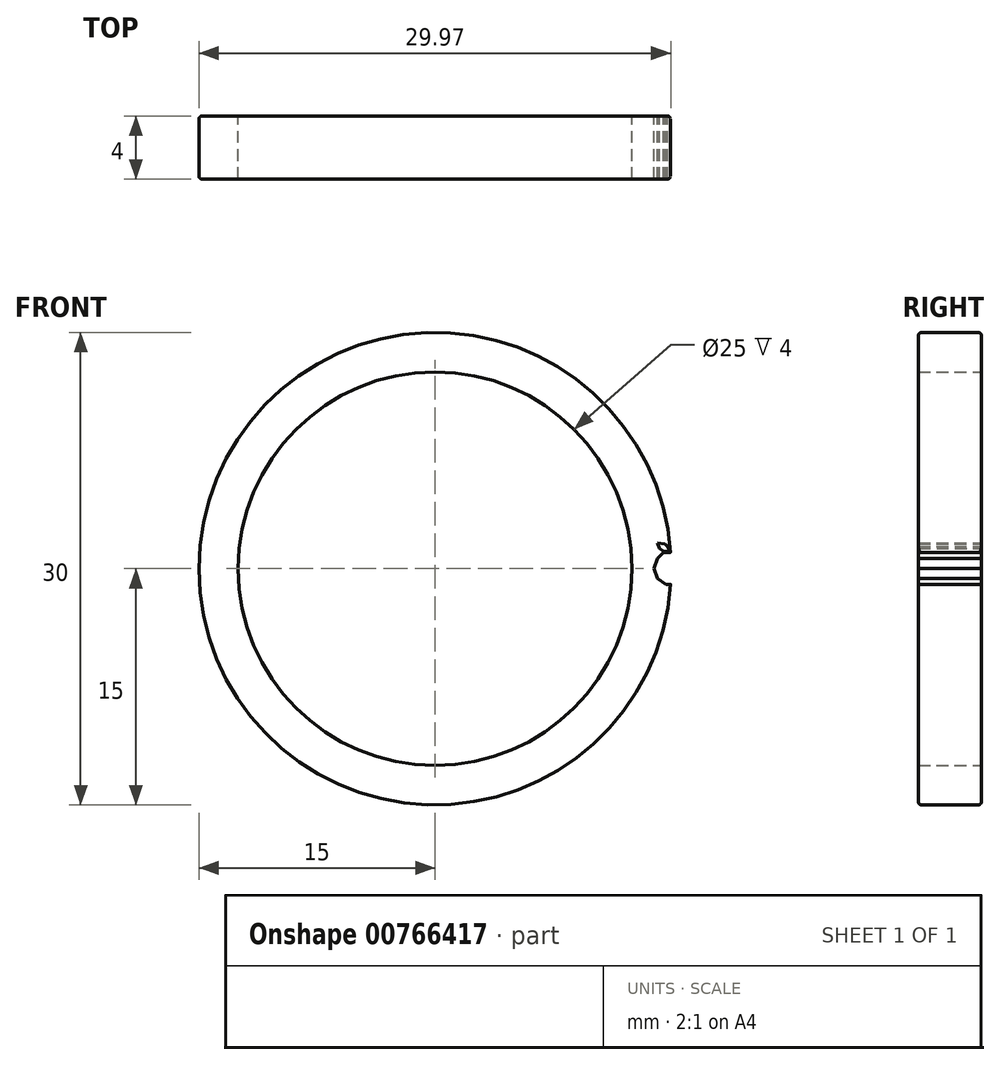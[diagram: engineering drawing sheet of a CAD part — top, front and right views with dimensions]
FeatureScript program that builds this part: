
annotation { "Feature Type Name" : "Feature", "Feature Type Description" : "" }
export const myFeature = defineFeature(function(context is Context, id is Id, definition is map)
    precondition{}
    {
        {
            var Q0;
            Q0=qCreatedBy(makeId("Front.planeOp"),FACE);
            var sketch = newSketch(context, id + "F0", { "sketchPlane" : qUnion([Q0])});
            skCircle(sketch, "E0", {"center": v(0, 0) * mm, "radius": 15 * mm});
            skCircle(sketch, "E1", {"center": v(0, 0) * mm, "radius": 12.5 * mm});
            skSolve(sketch);
        }
        {
            var Q0;
            Q0=qCreatedBy(makeId("Front.planeOp"),FACE);
            var sketch = newSketch(context, id + "F1", { "sketchPlane" : qUnion([Q0])});
            skLineSegment(sketch, "E2.0", {"start": v(14.65, -1) * mm, "end": v(14.12, -0.6) * mm});
            skLineSegment(sketch, "E2.1", {"start": v(14.12, -0.6) * mm, "end": v(13.9, 0.03) * mm});
            skLineSegment(sketch, "E2.2", {"start": v(13.9, 0.03) * mm, "end": v(14.12, 0.66) * mm});
            skLineSegment(sketch, "E2.3", {"start": v(14.12, 0.66) * mm, "end": v(14.5, 1.03) * mm});
            skLineSegment(sketch, "E2.5", {"start": v(15.42, 1.03) * mm, "end": v(15.86, 0.66) * mm});
            skLineSegment(sketch, "E2.6", {"start": v(15.86, 0.66) * mm, "end": v(16.07, 0.03) * mm});
            skLineSegment(sketch, "E2.7", {"start": v(16.07, 0.03) * mm, "end": v(15.86, -0.6) * mm});
            skLineSegment(sketch, "E2.8", {"start": v(15.86, -0.6) * mm, "end": v(15.32, -1) * mm});
            skLineSegment(sketch, "E2.9", {"start": v(15.32, -1) * mm, "end": v(14.65, -1) * mm});
            skLineSegment(sketch, "E3", {"start": v(14.5, 1.03) * mm, "end": v(14.99, 1.03) * mm});
            skLineSegment(sketch, "E4", {"start": v(14.99, 1.03) * mm, "end": v(15.42, 1.03) * mm});
            skLineSegment(sketch, "E5", {"start": v(14.93, 1.06) * mm, "end": v(14.77, 1.4) * mm});
            skLineSegment(sketch, "E6", {"start": v(14.77, 1.4) * mm, "end": v(14.6, 1.56) * mm});
            skLineSegment(sketch, "E7", {"start": v(14.6, 1.56) * mm, "end": v(14.13, 1.64) * mm});
            skLineSegment(sketch, "E8", {"start": v(14.13, 1.64) * mm, "end": v(14.25, 1.28) * mm});
            skLineSegment(sketch, "E9", {"start": v(14.25, 1.28) * mm, "end": v(14.53, 1.1) * mm});
            skLineSegment(sketch, "E10", {"start": v(14.53, 1.1) * mm, "end": v(14.93, 1.06) * mm});
            skLineSegment(sketch, "E11", {"start": v(15, 1.06) * mm, "end": v(15.36, 1.1) * mm});
            skLineSegment(sketch, "E12", {"start": v(15.36, 1.1) * mm, "end": v(15.57, 1.2) * mm});
            skLineSegment(sketch, "E13", {"start": v(15.57, 1.2) * mm, "end": v(15.81, 1.62) * mm});
            skLineSegment(sketch, "E14", {"start": v(15.81, 1.62) * mm, "end": v(15.43, 1.63) * mm});
            skLineSegment(sketch, "E15", {"start": v(15.43, 1.63) * mm, "end": v(15.17, 1.43) * mm});
            skLineSegment(sketch, "E16", {"start": v(15.17, 1.43) * mm, "end": v(15, 1.06) * mm});
            skSolve(sketch);
        }
        {
            var Q0;
            Q0 = qSketchRegion(id + "F0", true);
            extrude(context, id + "F2", {"entities" : qUnion([Q0]), "endBound" : BoundingType.SYMMETRIC, "depth" : 4 * mm, "offsetDistance" : 25 * mm});
        }
        {
            var Q0;
            Q0 = qSketchRegion(id + "F1", true);
            extrude(context, id + "F3", {"entities" : qUnion([Q0]), "endBound" : BoundingType.SYMMETRIC, "depth" : 4 * mm, "offsetDistance" : 25 * mm});
        }
        {
            var Q0;
            Q0=makeQuery(id+"F3.opExtrude","SWEPT_BODY",BODY,{"disambiguationData":[OSD([sQuery(id+"F1.wireOp",EDGE,"E2.0"),sQuery(id+"F1.wireOp",EDGE,"E2.1"),sQuery(id+"F1.wireOp",EDGE,"E2.2"),sQuery(id+"F1.wireOp",EDGE,"E2.3"),sQuery(id+"F1.wireOp",EDGE,"E2.5"),sQuery(id+"F1.wireOp",EDGE,"E2.6"),sQuery(id+"F1.wireOp",EDGE,"E2.7"),sQuery(id+"F1.wireOp",EDGE,"E2.8"),sQuery(id+"F1.wireOp",EDGE,"E2.9"),sQuery(id+"F1.wireOp",EDGE,"E3"),sQuery(id+"F1.wireOp",EDGE,"E4")])]});
            var Q1;
            Q1=makeQuery(id+"F3.opExtrude","SWEPT_BODY",BODY,{"disambiguationData":[OSD([sQuery(id+"F1.wireOp",EDGE,"E11"),sQuery(id+"F1.wireOp",EDGE,"E12"),sQuery(id+"F1.wireOp",EDGE,"E13"),sQuery(id+"F1.wireOp",EDGE,"E14"),sQuery(id+"F1.wireOp",EDGE,"E15"),sQuery(id+"F1.wireOp",EDGE,"E16")])]});
            var Q2;
            Q2=makeQuery(id+"F3.opExtrude","SWEPT_BODY",BODY,{"disambiguationData":[OSD([sQuery(id+"F1.wireOp",EDGE,"E5"),sQuery(id+"F1.wireOp",EDGE,"E6"),sQuery(id+"F1.wireOp",EDGE,"E7"),sQuery(id+"F1.wireOp",EDGE,"E8"),sQuery(id+"F1.wireOp",EDGE,"E9"),sQuery(id+"F1.wireOp",EDGE,"E10")])]});
            var Q3;
            Q3=makeQuery(id+"F2.opExtrude","SWEPT_BODY",BODY,{"disambiguationData":[OSD([sQuery(id+"F0.wireOp",EDGE,"E0"),sQuery(id+"F0.wireOp",EDGE,"E1")])]});
            booleanBodies(context, id + "F4", {"operationType" : BooleanOperationType.SUBTRACTION, "tools" : qUnion([Q0, Q1, Q2]), "targets" : qUnion([Q3])});
        }
        {
            var Q0;
            Q0=makeQuery(id+"F2.opExtrude","CAP_EDGE",EDGE,{"disambiguationData":[OSD([sQuery(id+"F0.wireOp",EDGE,"E0")])],"isStart":false});
            var Q1;
            Q1=makeQuery(id+"F2.opExtrude","CAP_EDGE",EDGE,{"disambiguationData":[OSD([sQuery(id+"F0.wireOp",EDGE,"E0")])],"isStart":true});
            fillet(context, id + "F5", {"entities" : qUnion([Q0, Q1]), "radius" : 0.2 * mm, "tangentPropagation" : true, "allowEdgeOverflow" : false});
        }
    });
